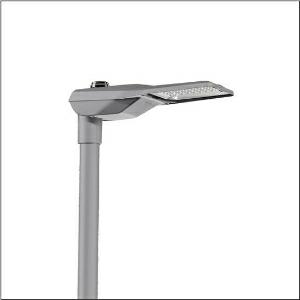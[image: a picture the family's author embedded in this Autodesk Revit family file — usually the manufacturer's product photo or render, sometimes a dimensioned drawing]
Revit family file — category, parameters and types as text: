
# Revit family: streetlight_sl_21_mini___st1_0a_5xe6d47n08gb_0bcc
name_source: partatom
category: Lighting Fixtures
units: mm (PartAtom-declared; Revit-internal decimal feet)

## family parameters
Cut with Voids When Loaded = No
Host = Face
Light Source = No
Part Type = Normal
Room Calculation Point = No
Round Connector Dimension = Use Diameter
Shared = No

## types (1)
- --- (1 x LED, 6180 lm, 40.4 W, 4000K)
    Apparent Load = 40 VA
    CIE Flux Codes = 37 72 97 100 100
    Color Rendering = 70
    Color Temperature = 4000K
    Default Elevation = 1800 mm
    Description = Streetlight SL 21 mini, mast luminaire, primary light control with lens, of PMMA, primary optical cover: cover, of toughened safety glass, transparent, light distribution: ST1.0a, light emission: direct distribution, primary light characteristic: asymmetric, installation type: side-entry, LED, 3G 1.5mm², High Power LED, rated luminous flux: 6.180lm, luminous efficacy: 153lm/W, light colour: 740, colour temperature: 4000K, control gear: NEMA (7pin), control: overheat protection, pre-setting: linear dimming characteristic, constant luminous flux control, time-dependent luminous flux control, flexible luminous flux parameterisation, mains connection: 230..240V, AC, 50/60Hz, connection cable pre-assembled, cable length: 8,5m, wiring characteristics: H07RN-F, start of lifetime: 40W, end of service life: 41W, reduction: 19W, luminaire housing, of diecast aluminium (EN AC-44300), powder-coated, SITECO metallic grey (DB 702S), corrosivity category C5 high according to DIN EN ISO 12944, multi-level sealing system, sealing non-destructively replaceable, inclination adjustable: 0°, 5°, 10°, 15°, length: 628mm, width: 235mm, height: 110mm, spigot size: 42mm (side-entry), mounting height: 4..8m, protection rating (complete): IP66, insulation class (complete): insulation class I (protective earthing), certification: CE, ENEC, ENEC+, VDE, impact resistance: IK10, permissible operating ambient temperature for outdoor applications: -40..+50°C, standard-compliant lighting for roads and squares, packaging unit: 1 piece

Light Distribution: ST1.0a
    Height = 110 mm
    Lamp = 1 x LED
    Lamp Light Flux = 6180 lm
    Lamp Power = 40.4 W
    Lamp count = 1
    Length = 625 mm
    Luminous efficacy = 153 lm/W
    Manufacturer = Siteco
    ModVariant = No
    Model = 5XE6D47N08GB
    Number of Poles = 1
    OnlyDefault = Yes
    Power Factor = 1
    Product Name = Streetlight SL 21 mini | ST1.0a
    Product group = mast luminaire | pylon top
    ProductGroupID = 6100
    Protection Class = Protection class I
    Protection Degree = IP 66
    RLX_Detail_Level = 1
    RLX_Emergency_Light_Flux = 0 lm
    RLX_Emergency_Type = 0
    RLX_Emergency_Type_DB = No
    RlxData = <blob elided: 25841 chars, md5=336bf26c>
    Socket = socket
    Standby Power = 0 W
    System Light Flux = 6180 lm
    System Power = 40 W
    Type Comments = factory setting: luminous flux: 100 % | dim-lin: 254 | 812 mA
    Type Image = l_1294379.jpg
    URL = http://relux.com
    VarID = @adj_135739
    Voltage = 0 V
    Weight = 0.00 kg
    Width = 234 mm

## geometry (parser evidence)
native form markers: Blend x4, Sweep x12
no freeform markers — native parametric forms only
